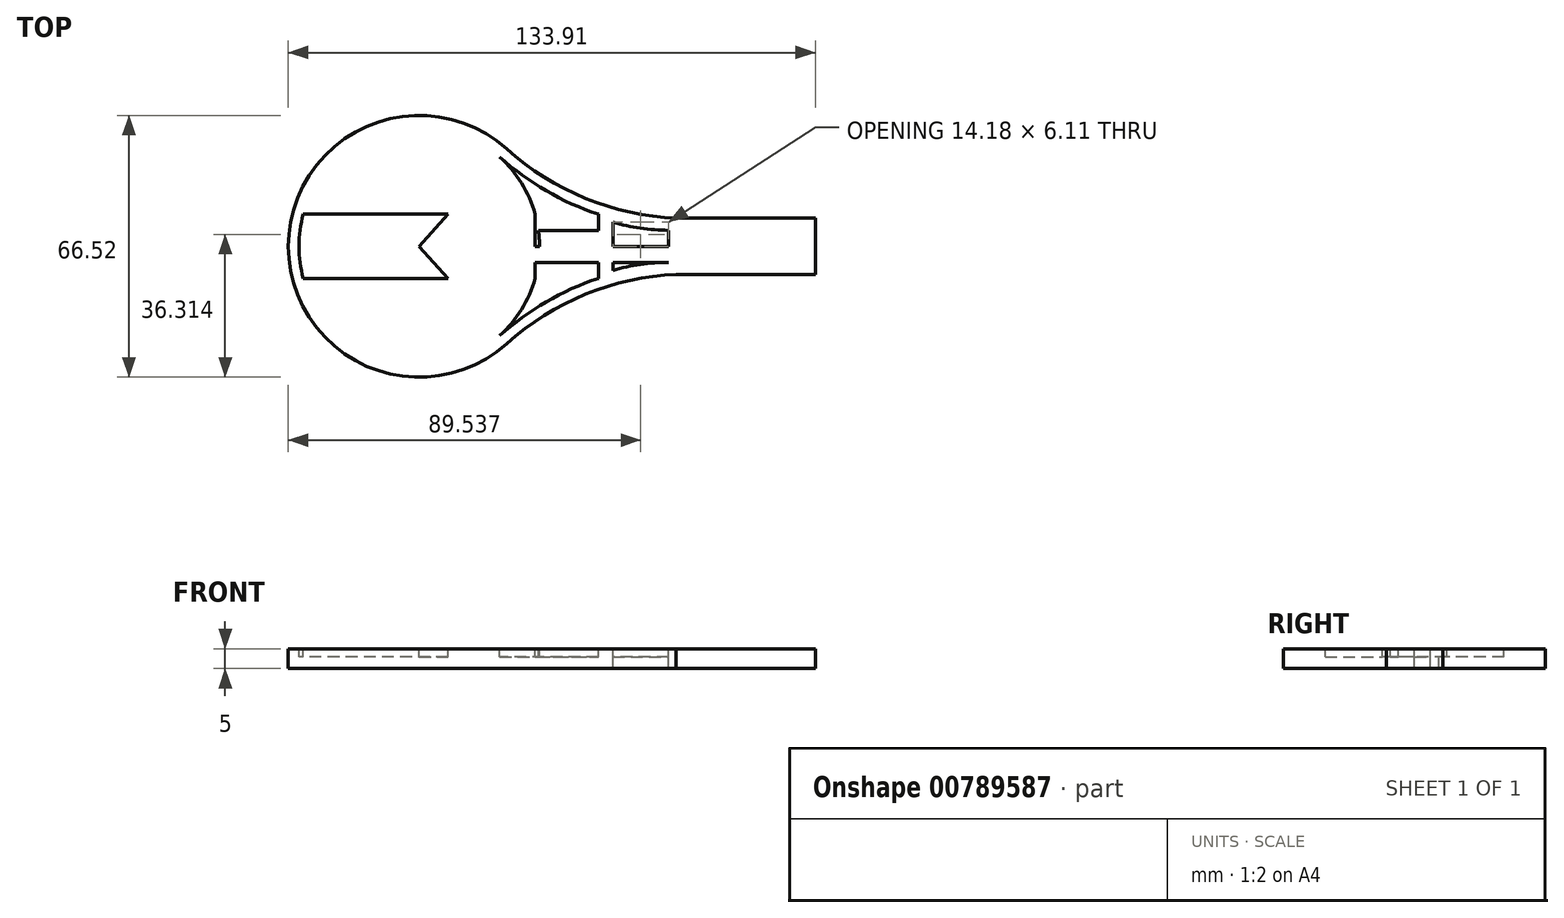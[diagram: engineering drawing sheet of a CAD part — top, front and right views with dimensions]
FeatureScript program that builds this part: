
annotation { "Feature Type Name" : "Feature", "Feature Type Description" : "" }
export const myFeature = defineFeature(function(context is Context, id is Id, definition is map)
    precondition{}
    {
        {
            var Q0;
            Q0=qCreatedBy(makeId("Top.planeOp"),FACE);
            var sketch = newSketch(context, id + "F0", { "sketchPlane" : qUnion([Q0])});
            skCircle(sketch, "E0", {"center": v(0, 0) * mm, "radius": 33.26 * mm});
            skLineSegment(sketch, "E1", {"start": v(0, 0) * mm, "end": v(100.65, 0) * mm});
            skLineSegment(sketch, "E2", {"start": v(100.65, 0) * mm, "end": v(0, 0) * mm});
            skLineSegment(sketch, "E3.bottom", {"start": v(29.96, 7.14) * mm, "end": v(-29.96, 7.14) * mm});
            skLineSegment(sketch, "E3.top", {"start": v(29.96, -7.14) * mm, "end": v(-29.96, -7.14) * mm});
            skLineSegment(sketch, "E3.left", {"start": v(29.96, 7.14) * mm, "end": v(29.96, -7.14) * mm});
            skLineSegment(sketch, "E3.right", {"start": v(-29.96, 7.14) * mm, "end": v(-29.96, -7.14) * mm});
            skLineSegment(sketch, "E4.bottom", {"start": v(29.96, 7.14) * mm, "end": v(100.65, 7.14) * mm});
            skLineSegment(sketch, "E4.top", {"start": v(29.96, 0) * mm, "end": v(100.65, 0) * mm});
            skLineSegment(sketch, "E4.left", {"start": v(29.96, 7.14) * mm, "end": v(29.96, 0) * mm});
            skLineSegment(sketch, "E4.right", {"start": v(100.65, 7.14) * mm, "end": v(100.65, 0) * mm});
            skLineSegment(sketch, "E5.bottom", {"start": v(29.96, -7.14) * mm, "end": v(100.65, -7.14) * mm});
            skLineSegment(sketch, "E5.left", {"start": v(29.96, -7.14) * mm, "end": v(29.96, 0) * mm});
            skLineSegment(sketch, "E5.right", {"start": v(100.65, -7.14) * mm, "end": v(100.65, 0) * mm});
            skLineSegment(sketch, "E6", {"start": v(65.3, 7.14) * mm, "end": v(65.3, -7.14) * mm});
            skLineSegment(sketch, "E7.bottom", {"start": v(0, 0) * mm, "end": v(0, 0) * mm});
            skLineSegment(sketch, "E7.top", {"start": v(0, 33.26) * mm, "end": v(0, 33.26) * mm});
            skLineSegment(sketch, "E7.left", {"start": v(0, 0) * mm, "end": v(0, 33.26) * mm});
            skLineSegment(sketch, "E7.right", {"start": v(0, 0) * mm, "end": v(0, 33.26) * mm});
            skLineSegment(sketch, "E8.top", {"start": v(0, -33.26) * mm, "end": v(0, -33.26) * mm});
            skLineSegment(sketch, "E8.left", {"start": v(0, 0) * mm, "end": v(0, -33.26) * mm});
            skLineSegment(sketch, "E8.right", {"start": v(0, 0) * mm, "end": v(0, -33.26) * mm});
            skPoint(sketch, "E9.oppositeSnap0", {"position": v(-29.96, 0) * mm});
            skLineSegment(sketch, "E9.bottom", {"start": v(0, 0) * mm, "end": v(-33.26, 0) * mm});
            skLineSegment(sketch, "E9.top", {"start": v(0, 0) * mm, "end": v(-33.26, 0) * mm});
            skLineSegment(sketch, "E9.right", {"start": v(-33.26, 0) * mm, "end": v(-33.26, 0) * mm});
            skLineSegment(sketch, "E10.top", {"start": v(0, 33.26) * mm, "end": v(-33.26, 33.26) * mm});
            skLineSegment(sketch, "E10.right", {"start": v(-33.26, 0) * mm, "end": v(-33.26, 33.26) * mm});
            skLineSegment(sketch, "E11.bottom", {"start": v(0, 0) * mm, "end": v(29.96, 0) * mm});
            skLineSegment(sketch, "E11.top", {"start": v(0, 33.26) * mm, "end": v(29.96, 33.26) * mm});
            skLineSegment(sketch, "E11.right", {"start": v(29.96, 0) * mm, "end": v(29.96, 33.26) * mm});
            skPoint(sketch, "E12.oppositeSnap0", {"position": v(29.96, 3.57) * mm});
            skLineSegment(sketch, "E12.top", {"start": v(0, -33.26) * mm, "end": v(29.96, -33.26) * mm});
            skLineSegment(sketch, "E12.right", {"start": v(29.96, 0) * mm, "end": v(29.96, -33.26) * mm});
            skLineSegment(sketch, "E13.top", {"start": v(0, -33.26) * mm, "end": v(-33.26, -33.26) * mm});
            skLineSegment(sketch, "E13.right", {"start": v(-33.26, 0) * mm, "end": v(-33.26, -33.26) * mm});
            skLineSegment(sketch, "E14", {"start": v(29.96, 33.26) * mm, "end": v(0, 0) * mm});
            skLineSegment(sketch, "E15", {"start": v(29.96, -33.26) * mm, "end": v(0, 0) * mm});
            skArc(sketch, "E16", {"start": v(22.26, 24.71) * mm, "mid": v(42.25, 12.17) * mm, "end": v(65.3, 7.14) * mm});
            skArc(sketch, "E17", {"start": v(65.3, -7.14) * mm, "mid": v(42.25, -12.17) * mm, "end": v(22.26, -24.71) * mm});
            skSolve(sketch);
        }
        {
            var Q0;
            {var subQ3=sQuery(id+"F0.wireOp",EDGE,"E3.bottom");var subQ5=sQuery(id+"F0.wireOp",EDGE,"E7.left");var subQ6=makeQuery(id+"F0.imprint","INTERSECT",VERTEX,{"derivedFrom":[subQ3,subQ5]});Q0=makeQuery(id+"F0.imprint","IMPRINT",FACE,{"disambiguationData":[TD([[makeQuery(id+"F0.imprint","IMPRINT",EDGE,{"disambiguationData":[TD([[subQ6,-1.0]])],"derivedFrom":subQ3}),-1.0]])]});}
            var Q1;
            {var subQ0=sQuery(id+"F0.wireOp",EDGE,"E8.left");var subQ1=sQuery(id+"F0.wireOp",EDGE,"E3.top");var subQ2=makeQuery(id+"F0.imprint","INTERSECT",VERTEX,{"derivedFrom":[subQ1,subQ0]});Q1=makeQuery(id+"F0.imprint","IMPRINT",FACE,{"disambiguationData":[TD([[makeQuery(id+"F0.imprint","IMPRINT",EDGE,{"disambiguationData":[TD([[subQ2,-1.0]])],"derivedFrom":subQ1}),1.0]])]});}
            var Q2;
            {var subQ0=sQuery(id+"F0.wireOp",EDGE,"E8.left");var subQ1=sQuery(id+"F0.wireOp",EDGE,"E3.top");var subQ2=makeQuery(id+"F0.imprint","INTERSECT",VERTEX,{"derivedFrom":[subQ1,subQ0]});Q2=makeQuery(id+"F0.imprint","IMPRINT",FACE,{"disambiguationData":[TD([[makeQuery(id+"F0.imprint","IMPRINT",EDGE,{"disambiguationData":[TD([[subQ2,-1.0]])],"derivedFrom":subQ1}),-1.0]])]});}
            var Q3;
            {var subQ0=sQuery(id+"F0.wireOp",EDGE,"E7.left");var subQ1=sQuery(id+"F0.wireOp",EDGE,"E3.bottom");var subQ2=makeQuery(id+"F0.imprint","INTERSECT",VERTEX,{"derivedFrom":[subQ1,subQ0]});Q3=makeQuery(id+"F0.imprint","IMPRINT",FACE,{"disambiguationData":[TD([[makeQuery(id+"F0.imprint","IMPRINT",EDGE,{"disambiguationData":[TD([[subQ2,-1.0]])],"derivedFrom":subQ1}),1.0]])]});}
            var Q4;
            {var subQ0=sQuery(id+"F0.wireOp",EDGE,"E8.left");var subQ5=sQuery(id+"F0.wireOp",EDGE,"E3.top");var subQ6=makeQuery(id+"F0.imprint","INTERSECT",VERTEX,{"derivedFrom":[subQ5,subQ0]});Q4=makeQuery(id+"F0.imprint","IMPRINT",FACE,{"disambiguationData":[TD([[makeQuery(id+"F0.imprint","IMPRINT",EDGE,{"disambiguationData":[TD([[subQ6,1.0]])],"derivedFrom":subQ5}),1.0]])]});}
            var Q5;
            {var subQ1=sQuery(id+"F0.wireOp",EDGE,"E0");var subQ3=sQuery(id+"F0.wireOp",EDGE,"E12.right");var subQ4=makeQuery(id+"F0.imprint","INTERSECT",VERTEX,{"derivedFrom":[subQ1,subQ3]});Q5=makeQuery(id+"F0.imprint","IMPRINT",FACE,{"disambiguationData":[TD([[makeQuery(id+"F0.imprint","IMPRINT",EDGE,{"disambiguationData":[TD([[subQ4,1.0]])],"derivedFrom":subQ1}),1.0]])]});}
            var Q6;
            {var subQ0=sQuery(id+"F0.wireOp",EDGE,"E8.left");var subQ1=sQuery(id+"F0.wireOp",EDGE,"E3.top");var subQ2=makeQuery(id+"F0.imprint","INTERSECT",VERTEX,{"derivedFrom":[subQ1,subQ0]});Q6=makeQuery(id+"F0.imprint","IMPRINT",FACE,{"disambiguationData":[TD([[makeQuery(id+"F0.imprint","IMPRINT",EDGE,{"disambiguationData":[TD([[subQ2,1.0]])],"derivedFrom":subQ1}),-1.0]])]});}
            var Q7;
            {var subQ3=sQuery(id+"F0.wireOp",EDGE,"E15");var subQ5=sQuery(id+"F0.wireOp",EDGE,"E3.top");var subQ6=makeQuery(id+"F0.imprint","INTERSECT",VERTEX,{"derivedFrom":[subQ5,subQ3]});Q7=makeQuery(id+"F0.imprint","IMPRINT",FACE,{"disambiguationData":[TD([[makeQuery(id+"F0.imprint","IMPRINT",EDGE,{"disambiguationData":[TD([[subQ6,1.0]])],"derivedFrom":subQ5}),-1.0]])]});}
            var Q8;
            {var subQ3=sQuery(id+"F0.wireOp",EDGE,"E14");var subQ5=sQuery(id+"F0.wireOp",EDGE,"E3.bottom");var subQ6=makeQuery(id+"F0.imprint","INTERSECT",VERTEX,{"derivedFrom":[subQ5,subQ3]});Q8=makeQuery(id+"F0.imprint","IMPRINT",FACE,{"disambiguationData":[TD([[makeQuery(id+"F0.imprint","IMPRINT",EDGE,{"disambiguationData":[TD([[subQ6,1.0]])],"derivedFrom":subQ5}),1.0]])]});}
            var Q9;
            {var subQ0=sQuery(id+"F0.wireOp",EDGE,"E7.left");var subQ1=sQuery(id+"F0.wireOp",EDGE,"E3.bottom");var subQ2=makeQuery(id+"F0.imprint","INTERSECT",VERTEX,{"derivedFrom":[subQ1,subQ0]});Q9=makeQuery(id+"F0.imprint","IMPRINT",FACE,{"disambiguationData":[TD([[makeQuery(id+"F0.imprint","IMPRINT",EDGE,{"disambiguationData":[TD([[subQ2,1.0]])],"derivedFrom":subQ1}),1.0]])]});}
            var Q10;
            {var subQ1=sQuery(id+"F0.wireOp",EDGE,"E0");var subQ3=sQuery(id+"F0.wireOp",EDGE,"E11.right");var subQ4=makeQuery(id+"F0.imprint","INTERSECT",VERTEX,{"derivedFrom":[subQ1,subQ3]});Q10=makeQuery(id+"F0.imprint","IMPRINT",FACE,{"disambiguationData":[TD([[makeQuery(id+"F0.imprint","IMPRINT",EDGE,{"disambiguationData":[TD([[subQ4,-1.0]])],"derivedFrom":subQ1}),1.0]])]});}
            var Q11;
            {var subQ0=sQuery(id+"F0.wireOp",EDGE,"E7.left");var subQ5=sQuery(id+"F0.wireOp",EDGE,"E3.bottom");var subQ6=makeQuery(id+"F0.imprint","INTERSECT",VERTEX,{"derivedFrom":[subQ5,subQ0]});Q11=makeQuery(id+"F0.imprint","IMPRINT",FACE,{"disambiguationData":[TD([[makeQuery(id+"F0.imprint","IMPRINT",EDGE,{"disambiguationData":[TD([[subQ6,1.0]])],"derivedFrom":subQ5}),-1.0]])]});}
            var Q12;
            {var subQ0=sQuery(id+"F0.wireOp",EDGE,"E16");var subQ3=sQuery(id+"F0.wireOp",EDGE,"E11.right");var subQ5=makeQuery(id+"F0.imprint","INTERSECT",VERTEX,{"derivedFrom":[subQ3,subQ0]});Q12=makeQuery(id+"F0.imprint","IMPRINT",FACE,{"disambiguationData":[TD([[makeQuery(id+"F0.imprint","IMPRINT",EDGE,{"disambiguationData":[TD([[subQ5,1.0]])],"derivedFrom":subQ3}),1.0]])]});}
            var Q13;
            {var subQ0=sQuery(id+"F0.wireOp",EDGE,"E17");var subQ3=sQuery(id+"F0.wireOp",EDGE,"E12.right");var subQ5=makeQuery(id+"F0.imprint","INTERSECT",VERTEX,{"derivedFrom":[subQ3,subQ0]});Q13=makeQuery(id+"F0.imprint","IMPRINT",FACE,{"disambiguationData":[TD([[makeQuery(id+"F0.imprint","IMPRINT",EDGE,{"disambiguationData":[TD([[subQ5,1.0]])],"derivedFrom":subQ3}),-1.0]])]});}
            var Q14;
            {var subQ0=sQuery(id+"F0.wireOp",EDGE,"E5.bottom");var subQ1=sQuery(id+"F0.wireOp",EDGE,"E0");var subQ2=makeQuery(id+"F0.imprint","INTERSECT",VERTEX,{"derivedFrom":[subQ1,subQ0]});Q14=makeQuery(id+"F0.imprint","IMPRINT",FACE,{"disambiguationData":[TD([[makeQuery(id+"F0.imprint","IMPRINT",EDGE,{"disambiguationData":[TD([[subQ2,1.0]])],"derivedFrom":subQ1}),1.0]])]});}
            var Q15;
            {var subQ0=sQuery(id+"F0.wireOp",EDGE,"E1");var subQ1=sQuery(id+"F0.wireOp",EDGE,"E0");var subQ2=makeQuery(id+"F0.imprint","INTERSECT",VERTEX,{"derivedFrom":[subQ1,subQ0]});Q15=makeQuery(id+"F0.imprint","IMPRINT",FACE,{"disambiguationData":[TD([[makeQuery(id+"F0.imprint","IMPRINT",EDGE,{"disambiguationData":[TD([[subQ2,1.0]])],"derivedFrom":subQ1}),1.0]])]});}
            var Q16;
            {var subQ0=sQuery(id+"F0.wireOp",EDGE,"E1");var subQ1=sQuery(id+"F0.wireOp",EDGE,"E0");var subQ2=makeQuery(id+"F0.imprint","INTERSECT",VERTEX,{"derivedFrom":[subQ1,subQ0]});Q16=makeQuery(id+"F0.imprint","IMPRINT",FACE,{"disambiguationData":[TD([[makeQuery(id+"F0.imprint","IMPRINT",EDGE,{"disambiguationData":[TD([[subQ2,-1.0]])],"derivedFrom":subQ1}),1.0]])]});}
            var Q17;
            {var subQ0=sQuery(id+"F0.wireOp",EDGE,"E4.bottom");var subQ1=sQuery(id+"F0.wireOp",EDGE,"E0");var subQ2=makeQuery(id+"F0.imprint","INTERSECT",VERTEX,{"derivedFrom":[subQ1,subQ0]});Q17=makeQuery(id+"F0.imprint","IMPRINT",FACE,{"disambiguationData":[TD([[makeQuery(id+"F0.imprint","IMPRINT",EDGE,{"disambiguationData":[TD([[subQ2,-1.0]])],"derivedFrom":subQ1}),1.0]])]});}
            var Q18;
            {var subQ0=sQuery(id+"F0.wireOp",EDGE,"E4.bottom");var subQ1=sQuery(id+"F0.wireOp",EDGE,"E0");var subQ2=makeQuery(id+"F0.imprint","INTERSECT",VERTEX,{"derivedFrom":[subQ1,subQ0]});Q18=makeQuery(id+"F0.imprint","IMPRINT",FACE,{"disambiguationData":[TD([[makeQuery(id+"F0.imprint","IMPRINT",EDGE,{"disambiguationData":[TD([[subQ2,-1.0]])],"derivedFrom":subQ1}),-1.0]])]});}
            var Q19;
            {var subQ0=sQuery(id+"F0.wireOp",EDGE,"E1");var subQ1=sQuery(id+"F0.wireOp",EDGE,"E0");var subQ2=makeQuery(id+"F0.imprint","INTERSECT",VERTEX,{"derivedFrom":[subQ1,subQ0]});Q19=makeQuery(id+"F0.imprint","IMPRINT",FACE,{"disambiguationData":[TD([[makeQuery(id+"F0.imprint","IMPRINT",EDGE,{"disambiguationData":[TD([[subQ2,-1.0]])],"derivedFrom":subQ1}),-1.0]])]});}
            var Q20;
            {var subQ0=sQuery(id+"F0.wireOp",EDGE,"E1");var subQ1=sQuery(id+"F0.wireOp",EDGE,"E0");var subQ2=makeQuery(id+"F0.imprint","INTERSECT",VERTEX,{"derivedFrom":[subQ1,subQ0]});Q20=makeQuery(id+"F0.imprint","IMPRINT",FACE,{"disambiguationData":[TD([[makeQuery(id+"F0.imprint","IMPRINT",EDGE,{"disambiguationData":[TD([[subQ2,1.0]])],"derivedFrom":subQ1}),-1.0]])]});}
            var Q21;
            {var subQ0=sQuery(id+"F0.wireOp",EDGE,"E5.bottom");var subQ1=sQuery(id+"F0.wireOp",EDGE,"E0");var subQ2=makeQuery(id+"F0.imprint","INTERSECT",VERTEX,{"derivedFrom":[subQ1,subQ0]});Q21=makeQuery(id+"F0.imprint","IMPRINT",FACE,{"disambiguationData":[TD([[makeQuery(id+"F0.imprint","IMPRINT",EDGE,{"disambiguationData":[TD([[subQ2,1.0]])],"derivedFrom":subQ1}),-1.0]])]});}
            var Q22;
            {var subQ3=sQuery(id+"F0.wireOp",EDGE,"E5.right");Q22=makeQuery(id+"F0.imprint","IMPRINT",FACE,{"disambiguationData":[TD([[makeQuery(id+"F0.imprint","IMPRINT",EDGE,{"derivedFrom":subQ3}),1.0]])]});}
            var Q23;
            {var subQ3=sQuery(id+"F0.wireOp",EDGE,"E4.right");Q23=makeQuery(id+"F0.imprint","IMPRINT",FACE,{"disambiguationData":[TD([[makeQuery(id+"F0.imprint","IMPRINT",EDGE,{"derivedFrom":subQ3}),-1.0]])]});}
            extrude(context, id + "F1", {"entities" : qUnion([Q0, Q1, Q2, Q3, Q4, Q5, Q6, Q7, Q8, Q9, Q10, Q11, Q12, Q13, Q14, Q15, Q16, Q17, Q18, Q19, Q20, Q21, Q22, Q23]), "depth" : 5 * mm, "offsetDistance" : 25 * mm});
        }
        {
            var Q0;
            Q0=makeQuery(id+"F1.opExtrude","CAP_FACE",FACE,{"disambiguationData":[OSD([sQuery(id+"F0.wireOp",EDGE,"E0"),sQuery(id+"F0.wireOp",EDGE,"E4.bottom"),sQuery(id+"F0.wireOp",EDGE,"E4.right"),sQuery(id+"F0.wireOp",EDGE,"E5.bottom"),sQuery(id+"F0.wireOp",EDGE,"E5.right"),sQuery(id+"F0.wireOp",EDGE,"E16"),sQuery(id+"F0.wireOp",EDGE,"E17")])],"isStart":false});
            var sketch = newSketch(context, id + "F2", { "sketchPlane" : qUnion([Q0])});
            skCircle(sketch, "E18", {"center": v(0, 0) * mm, "radius": 30.56 * mm});
            skLineSegment(sketch, "E19", {"start": v(0, 0) * mm, "end": v(22.26, 24.71) * mm});
            skLineSegment(sketch, "E20", {"start": v(22.26, 24.71) * mm, "end": v(0, 0) * mm});
            skLineSegment(sketch, "E21", {"start": v(0, 0) * mm, "end": v(22.26, -24.71) * mm});
            skLineSegment(sketch, "E22", {"start": v(22.26, -24.71) * mm, "end": v(0, 0) * mm});
            skLineSegment(sketch, "E23.bottom", {"start": v(29.45, 8.15) * mm, "end": v(-29.45, 8.15) * mm});
            skLineSegment(sketch, "E23.top", {"start": v(29.45, -8.15) * mm, "end": v(-29.45, -8.15) * mm});
            skLineSegment(sketch, "E23.left", {"start": v(29.45, 8.15) * mm, "end": v(29.45, -8.15) * mm});
            skLineSegment(sketch, "E23.right", {"start": v(-29.45, 8.15) * mm, "end": v(-29.45, -8.15) * mm});
            skLineSegment(sketch, "E24", {"start": v(0, 0) * mm, "end": v(45.57, 0) * mm});
            skLineSegment(sketch, "E25", {"start": v(45.57, 0) * mm, "end": v(0, 0) * mm});
            skLineSegment(sketch, "E26.bottom", {"start": v(29.45, 8.15) * mm, "end": v(45.57, 8.15) * mm});
            skLineSegment(sketch, "E26.top", {"start": v(29.45, 0) * mm, "end": v(45.57, 0) * mm});
            skLineSegment(sketch, "E26.left", {"start": v(29.45, 8.15) * mm, "end": v(29.45, 0) * mm});
            skLineSegment(sketch, "E26.right", {"start": v(45.57, 8.15) * mm, "end": v(45.57, 0) * mm});
            skLineSegment(sketch, "E27.bottom", {"start": v(29.45, -8.15) * mm, "end": v(45.57, -8.15) * mm});
            skLineSegment(sketch, "E27.left", {"start": v(29.45, -8.15) * mm, "end": v(29.45, 0) * mm});
            skLineSegment(sketch, "E27.right", {"start": v(45.57, -8.15) * mm, "end": v(45.57, 0) * mm});
            skArc(sketch, "E28", {"start": v(20.45, 22.7) * mm, "mid": v(32.25, 14.11) * mm, "end": v(45.57, 8.15) * mm});
            skArc(sketch, "E29", {"start": v(45.57, -8.15) * mm, "mid": v(32.25, -14.11) * mm, "end": v(20.45, -22.7) * mm});
            skLineSegment(sketch, "E30.bottom", {"start": v(25.69, 4.07) * mm, "end": v(-25.69, 4.07) * mm});
            skLineSegment(sketch, "E30.top", {"start": v(25.69, -4.07) * mm, "end": v(-25.69, -4.07) * mm});
            skLineSegment(sketch, "E30.left", {"start": v(25.69, 4.07) * mm, "end": v(25.69, -4.07) * mm});
            skLineSegment(sketch, "E30.right", {"start": v(-25.69, 4.07) * mm, "end": v(-25.69, -4.07) * mm});
            skPoint(sketch, "E30.cornerSnap0", {"position": v(29.45, 4.07) * mm});
            skLineSegment(sketch, "E31", {"start": v(0, 0) * mm, "end": v(63.37, 0) * mm});
            skLineSegment(sketch, "E32", {"start": v(63.37, 0) * mm, "end": v(0, 0) * mm});
            skLineSegment(sketch, "E33.bottom", {"start": v(25.69, 4.07) * mm, "end": v(63.37, 4.07) * mm});
            skLineSegment(sketch, "E33.top", {"start": v(25.69, 0) * mm, "end": v(63.37, 0) * mm});
            skLineSegment(sketch, "E33.left", {"start": v(25.69, 4.07) * mm, "end": v(25.69, 0) * mm});
            skLineSegment(sketch, "E33.right", {"start": v(63.37, 4.07) * mm, "end": v(63.37, 0) * mm});
            skLineSegment(sketch, "E34.bottom", {"start": v(25.69, -4.07) * mm, "end": v(63.37, -4.07) * mm});
            skLineSegment(sketch, "E34.left", {"start": v(25.69, -4.07) * mm, "end": v(25.69, 0) * mm});
            skLineSegment(sketch, "E34.right", {"start": v(63.37, -4.07) * mm, "end": v(63.37, 0) * mm});
            skLineSegment(sketch, "E35", {"start": v(0, 0) * mm, "end": v(49.19, 0) * mm});
            skLineSegment(sketch, "E36", {"start": v(49.19, 0) * mm, "end": v(0, 0) * mm});
            skLineSegment(sketch, "E37.bottom", {"start": v(45.57, 8.15) * mm, "end": v(49.19, 8.15) * mm});
            skLineSegment(sketch, "E37.top", {"start": v(45.57, 0) * mm, "end": v(49.19, 0) * mm});
            skLineSegment(sketch, "E37.right", {"start": v(49.19, 8.15) * mm, "end": v(49.19, 0) * mm});
            skLineSegment(sketch, "E38.bottom", {"start": v(45.57, -8.15) * mm, "end": v(49.19, -8.15) * mm});
            skLineSegment(sketch, "E38.right", {"start": v(49.19, -8.15) * mm, "end": v(49.19, 0) * mm});
            skLineSegment(sketch, "E39.bottom", {"start": v(45.57, 4.07) * mm, "end": v(49.19, 4.07) * mm});
            skLineSegment(sketch, "E39.left", {"start": v(45.57, 4.07) * mm, "end": v(45.57, 0) * mm});
            skLineSegment(sketch, "E39.right", {"start": v(49.19, 4.07) * mm, "end": v(49.19, 0) * mm});
            skLineSegment(sketch, "E40.bottom", {"start": v(45.57, -4.07) * mm, "end": v(49.19, -4.07) * mm});
            skLineSegment(sketch, "E40.left", {"start": v(45.57, -4.07) * mm, "end": v(45.57, 0) * mm});
            skLineSegment(sketch, "E40.right", {"start": v(49.19, -4.07) * mm, "end": v(49.19, 0) * mm});
            skLineSegment(sketch, "E41.left", {"start": v(45.57, 4.07) * mm, "end": v(45.57, 8.15) * mm});
            skLineSegment(sketch, "E41.right", {"start": v(49.19, 4.07) * mm, "end": v(49.19, 8.15) * mm});
            skLineSegment(sketch, "E42.left", {"start": v(45.57, -4.07) * mm, "end": v(45.57, -8.15) * mm});
            skLineSegment(sketch, "E42.right", {"start": v(49.19, -4.07) * mm, "end": v(49.19, -8.15) * mm});
            skLineSegment(sketch, "E43", {"start": v(49.19, 6.1) * mm, "end": v(45.57, 5.94) * mm});
            skLineSegment(sketch, "E44", {"start": v(45.57, 5.94) * mm, "end": v(49.19, 6.1) * mm});
            skLineSegment(sketch, "E45", {"start": v(49.19, -6.1) * mm, "end": v(45.57, -5.94) * mm});
            skLineSegment(sketch, "E46", {"start": v(45.57, -5.94) * mm, "end": v(49.19, -6.1) * mm});
            skArc(sketch, "E47", {"start": v(49.19, 6.1) * mm, "mid": v(56.2, 4.58) * mm, "end": v(63.37, 4.07) * mm});
            skArc(sketch, "E48", {"start": v(63.37, -4.07) * mm, "mid": v(56.2, -4.58) * mm, "end": v(49.19, -6.1) * mm});
            skSolve(sketch);
        }
        {
            var Q0;
            {var subQ0=sQuery(id+"F2.wireOp",EDGE,"E23.bottom");var subQ3=sQuery(id+"F2.wireOp",EDGE,"E20");var subQ5=makeQuery(id+"F2.imprint","INTERSECT",VERTEX,{"derivedFrom":[subQ3,subQ0]});Q0=makeQuery(id+"F2.imprint","IMPRINT",FACE,{"disambiguationData":[TD([[makeQuery(id+"F2.imprint","IMPRINT",EDGE,{"disambiguationData":[TD([[subQ5,1.0]])],"derivedFrom":subQ3}),-1.0]])]});}
            var Q1;
            {var subQ0=sQuery(id+"F2.wireOp",EDGE,"E23.bottom");var subQ3=sQuery(id+"F2.wireOp",EDGE,"E20");var subQ5=makeQuery(id+"F2.imprint","INTERSECT",VERTEX,{"derivedFrom":[subQ3,subQ0]});Q1=makeQuery(id+"F2.imprint","IMPRINT",FACE,{"disambiguationData":[TD([[makeQuery(id+"F2.imprint","IMPRINT",EDGE,{"disambiguationData":[TD([[subQ5,1.0]])],"derivedFrom":subQ3}),1.0]])]});}
            var Q2;
            {var subQ0=sQuery(id+"F2.wireOp",EDGE,"E23.right");Q2=makeQuery(id+"F2.imprint","IMPRINT",FACE,{"disambiguationData":[TD([[makeQuery(id+"F2.imprint","IMPRINT",EDGE,{"derivedFrom":subQ0}),1.0]])]});}
            var Q3;
            {var subQ3=sQuery(id+"F2.wireOp",EDGE,"E20");var subQ6=sQuery(id+"F2.wireOp",EDGE,"E23.bottom");var subQ9=makeQuery(id+"F2.imprint","INTERSECT",VERTEX,{"derivedFrom":[subQ3,subQ6]});Q3=makeQuery(id+"F2.imprint","IMPRINT",FACE,{"disambiguationData":[TD([[makeQuery(id+"F2.imprint","IMPRINT",EDGE,{"disambiguationData":[TD([[subQ9,-1.0]])],"derivedFrom":subQ3}),1.0]])]});}
            var Q4;
            {var subQ3=sQuery(id+"F2.wireOp",EDGE,"E22");var subQ6=sQuery(id+"F2.wireOp",EDGE,"E23.top");var subQ9=makeQuery(id+"F2.imprint","INTERSECT",VERTEX,{"derivedFrom":[subQ3,subQ6]});Q4=makeQuery(id+"F2.imprint","IMPRINT",FACE,{"disambiguationData":[TD([[makeQuery(id+"F2.imprint","IMPRINT",EDGE,{"disambiguationData":[TD([[subQ9,-1.0]])],"derivedFrom":subQ3}),-1.0]])]});}
            var Q5;
            {var subQ5=sQuery(id+"F2.wireOp",EDGE,"E34.left");Q5=makeQuery(id+"F2.imprint","IMPRINT",FACE,{"disambiguationData":[TD([[makeQuery(id+"F2.imprint","IMPRINT",EDGE,{"derivedFrom":subQ5}),1.0]])]});}
            var Q6;
            {var subQ5=sQuery(id+"F2.wireOp",EDGE,"E33.left");Q6=makeQuery(id+"F2.imprint","IMPRINT",FACE,{"disambiguationData":[TD([[makeQuery(id+"F2.imprint","IMPRINT",EDGE,{"derivedFrom":subQ5}),-1.0]])]});}
            var Q7;
            {var subQ0=sQuery(id+"F2.wireOp",EDGE,"E30.right");Q7=makeQuery(id+"F2.imprint","IMPRINT",FACE,{"disambiguationData":[TD([[makeQuery(id+"F2.imprint","IMPRINT",EDGE,{"derivedFrom":subQ0}),1.0]])]});}
            var Q8;
            {var subQ0=sQuery(id+"F2.wireOp",EDGE,"E23.top");var subQ3=sQuery(id+"F2.wireOp",EDGE,"E22");var subQ5=makeQuery(id+"F2.imprint","INTERSECT",VERTEX,{"derivedFrom":[subQ3,subQ0]});Q8=makeQuery(id+"F2.imprint","IMPRINT",FACE,{"disambiguationData":[TD([[makeQuery(id+"F2.imprint","IMPRINT",EDGE,{"disambiguationData":[TD([[subQ5,1.0]])],"derivedFrom":subQ3}),1.0]])]});}
            var Q9;
            {var subQ0=sQuery(id+"F2.wireOp",EDGE,"E23.top");var subQ3=sQuery(id+"F2.wireOp",EDGE,"E22");var subQ5=makeQuery(id+"F2.imprint","INTERSECT",VERTEX,{"derivedFrom":[subQ3,subQ0]});Q9=makeQuery(id+"F2.imprint","IMPRINT",FACE,{"disambiguationData":[TD([[makeQuery(id+"F2.imprint","IMPRINT",EDGE,{"disambiguationData":[TD([[subQ5,1.0]])],"derivedFrom":subQ3}),-1.0]])]});}
            var Q10;
            {var subQ5=sQuery(id+"F2.wireOp",EDGE,"E34.left");Q10=makeQuery(id+"F2.imprint","IMPRINT",FACE,{"disambiguationData":[TD([[makeQuery(id+"F2.imprint","IMPRINT",EDGE,{"derivedFrom":subQ5}),-1.0]])]});}
            var Q11;
            {var subQ5=sQuery(id+"F2.wireOp",EDGE,"E33.left");Q11=makeQuery(id+"F2.imprint","IMPRINT",FACE,{"disambiguationData":[TD([[makeQuery(id+"F2.imprint","IMPRINT",EDGE,{"derivedFrom":subQ5}),1.0]])]});}
            var Q12;
            {var subQ0=sQuery(id+"F2.wireOp",EDGE,"E33.bottom");var subQ1=sQuery(id+"F2.wireOp",EDGE,"E18");var subQ2=makeQuery(id+"F2.imprint","INTERSECT",VERTEX,{"derivedFrom":[subQ1,subQ0]});Q12=makeQuery(id+"F2.imprint","IMPRINT",FACE,{"disambiguationData":[TD([[makeQuery(id+"F2.imprint","IMPRINT",EDGE,{"disambiguationData":[TD([[subQ2,1.0]])],"derivedFrom":subQ1}),1.0]])]});}
            var Q13;
            {var subQ0=sQuery(id+"F2.wireOp",EDGE,"E36");var subQ1=sQuery(id+"F2.wireOp",EDGE,"E18");var subQ2=makeQuery(id+"F2.imprint","INTERSECT",VERTEX,{"derivedFrom":[subQ1,subQ0]});Q13=makeQuery(id+"F2.imprint","IMPRINT",FACE,{"disambiguationData":[TD([[makeQuery(id+"F2.imprint","IMPRINT",EDGE,{"disambiguationData":[TD([[subQ2,1.0]])],"derivedFrom":subQ1}),1.0]])]});}
            var Q14;
            {var subQ1=sQuery(id+"F2.wireOp",EDGE,"E18");var subQ3=sQuery(id+"F2.wireOp",EDGE,"E34.bottom");var subQ4=makeQuery(id+"F2.imprint","INTERSECT",VERTEX,{"derivedFrom":[subQ1,subQ3]});Q14=makeQuery(id+"F2.imprint","IMPRINT",FACE,{"disambiguationData":[TD([[makeQuery(id+"F2.imprint","IMPRINT",EDGE,{"disambiguationData":[TD([[subQ4,1.0]])],"derivedFrom":subQ3}),-1.0]])]});}
            var Q15;
            {var subQ1=sQuery(id+"F2.wireOp",EDGE,"E18");var subQ3=sQuery(id+"F2.wireOp",EDGE,"E33.bottom");var subQ4=makeQuery(id+"F2.imprint","INTERSECT",VERTEX,{"derivedFrom":[subQ1,subQ3]});Q15=makeQuery(id+"F2.imprint","IMPRINT",FACE,{"disambiguationData":[TD([[makeQuery(id+"F2.imprint","IMPRINT",EDGE,{"disambiguationData":[TD([[subQ4,1.0]])],"derivedFrom":subQ3}),1.0]])]});}
            var Q16;
            {var subQ0=sQuery(id+"F2.wireOp",EDGE,"E26.bottom");Q16=makeQuery(id+"F2.imprint","IMPRINT",FACE,{"disambiguationData":[TD([[makeQuery(id+"F2.imprint","IMPRINT",EDGE,{"derivedFrom":subQ0}),1.0]])]});}
            var Q17;
            {var subQ6=sQuery(id+"F2.wireOp",EDGE,"E26.bottom");Q17=makeQuery(id+"F2.imprint","IMPRINT",FACE,{"disambiguationData":[TD([[makeQuery(id+"F2.imprint","IMPRINT",EDGE,{"derivedFrom":subQ6}),-1.0]])]});}
            var Q18;
            {var subQ5=sQuery(id+"F2.wireOp",EDGE,"E39.left");Q18=makeQuery(id+"F2.imprint","IMPRINT",FACE,{"disambiguationData":[TD([[makeQuery(id+"F2.imprint","IMPRINT",EDGE,{"derivedFrom":subQ5}),-1.0]])]});}
            var Q19;
            {var subQ5=sQuery(id+"F2.wireOp",EDGE,"E40.left");Q19=makeQuery(id+"F2.imprint","IMPRINT",FACE,{"disambiguationData":[TD([[makeQuery(id+"F2.imprint","IMPRINT",EDGE,{"derivedFrom":subQ5}),1.0]])]});}
            var Q20;
            {var subQ6=sQuery(id+"F2.wireOp",EDGE,"E27.bottom");Q20=makeQuery(id+"F2.imprint","IMPRINT",FACE,{"disambiguationData":[TD([[makeQuery(id+"F2.imprint","IMPRINT",EDGE,{"derivedFrom":subQ6}),1.0]])]});}
            var Q21;
            {var subQ0=sQuery(id+"F2.wireOp",EDGE,"E27.bottom");Q21=makeQuery(id+"F2.imprint","IMPRINT",FACE,{"disambiguationData":[TD([[makeQuery(id+"F2.imprint","IMPRINT",EDGE,{"derivedFrom":subQ0}),-1.0]])]});}
            var Q22;
            {var subQ0=sQuery(id+"F2.wireOp",EDGE,"E48");Q22=makeQuery(id+"F2.imprint","IMPRINT",FACE,{"disambiguationData":[TD([[makeQuery(id+"F2.imprint","IMPRINT",EDGE,{"derivedFrom":subQ0}),-1.0]])]});}
            var Q23;
            Q23=makeQuery(id+"F2.imprint","IMPRINT",FACE,{"disambiguationData":[TD([[makeQuery(id+"F2.imprint","IMPRINT",EDGE,{"derivedFrom":sQuery(id+"F2.wireOp",EDGE,"E33.top")}),-1.0]])]});
            var Q24;
            {var subQ0=sQuery(id+"F2.wireOp",EDGE,"E33.right");Q24=makeQuery(id+"F2.imprint","IMPRINT",FACE,{"disambiguationData":[TD([[makeQuery(id+"F2.imprint","IMPRINT",EDGE,{"derivedFrom":subQ0}),-1.0]])]});}
            var Q25;
            {var subQ0=sQuery(id+"F2.wireOp",EDGE,"E47");Q25=makeQuery(id+"F2.imprint","IMPRINT",FACE,{"disambiguationData":[TD([[makeQuery(id+"F2.imprint","IMPRINT",EDGE,{"derivedFrom":subQ0}),-1.0]])]});}
            var Q26;
            {var subQ0=sQuery(id+"F2.wireOp",EDGE,"E23.right");Q26=makeQuery(id+"F2.imprint","IMPRINT",FACE,{"disambiguationData":[TD([[makeQuery(id+"F2.imprint","IMPRINT",EDGE,{"derivedFrom":subQ0}),-1.0]])]});}
            extrude(context, id + "F3", {"entities" : qUnion([Q0, Q1, Q2, Q3, Q4, Q5, Q6, Q7, Q8, Q9, Q10, Q11, Q12, Q13, Q14, Q15, Q16, Q17, Q18, Q19, Q20, Q21, Q22, Q23, Q24, Q25, Q26]), "operationType" : NewBodyOperationType.REMOVE, "oppositeDirection" : true, "depth" : 2 * mm, "offsetDistance" : 25 * mm});
        }
        {
            var Q0;
            Q0=makeQuery(id+"F3.boolean.opBoolean","COPY",FACE,{"derivedFrom":makeQuery(id+"F3.opExtrude","CAP_FACE",FACE,{"disambiguationData":[OSD([sQuery(id+"F2.wireOp",EDGE,"E33.right"),sQuery(id+"F2.wireOp",EDGE,"E34.right"),sQuery(id+"F2.wireOp",EDGE,"E39.right"),sQuery(id+"F2.wireOp",EDGE,"E40.right"),sQuery(id+"F2.wireOp",EDGE,"E41.right"),sQuery(id+"F2.wireOp",EDGE,"E42.right"),sQuery(id+"F2.wireOp",EDGE,"E47"),sQuery(id+"F2.wireOp",EDGE,"E48")])],"isStart":false})});
            extrude(context, id + "F4", {"entities" : qUnion([Q0]), "operationType" : NewBodyOperationType.REMOVE, "oppositeDirection" : true, "depth" : 25 * mm, "offsetDistance" : 25 * mm});
        }
    });
